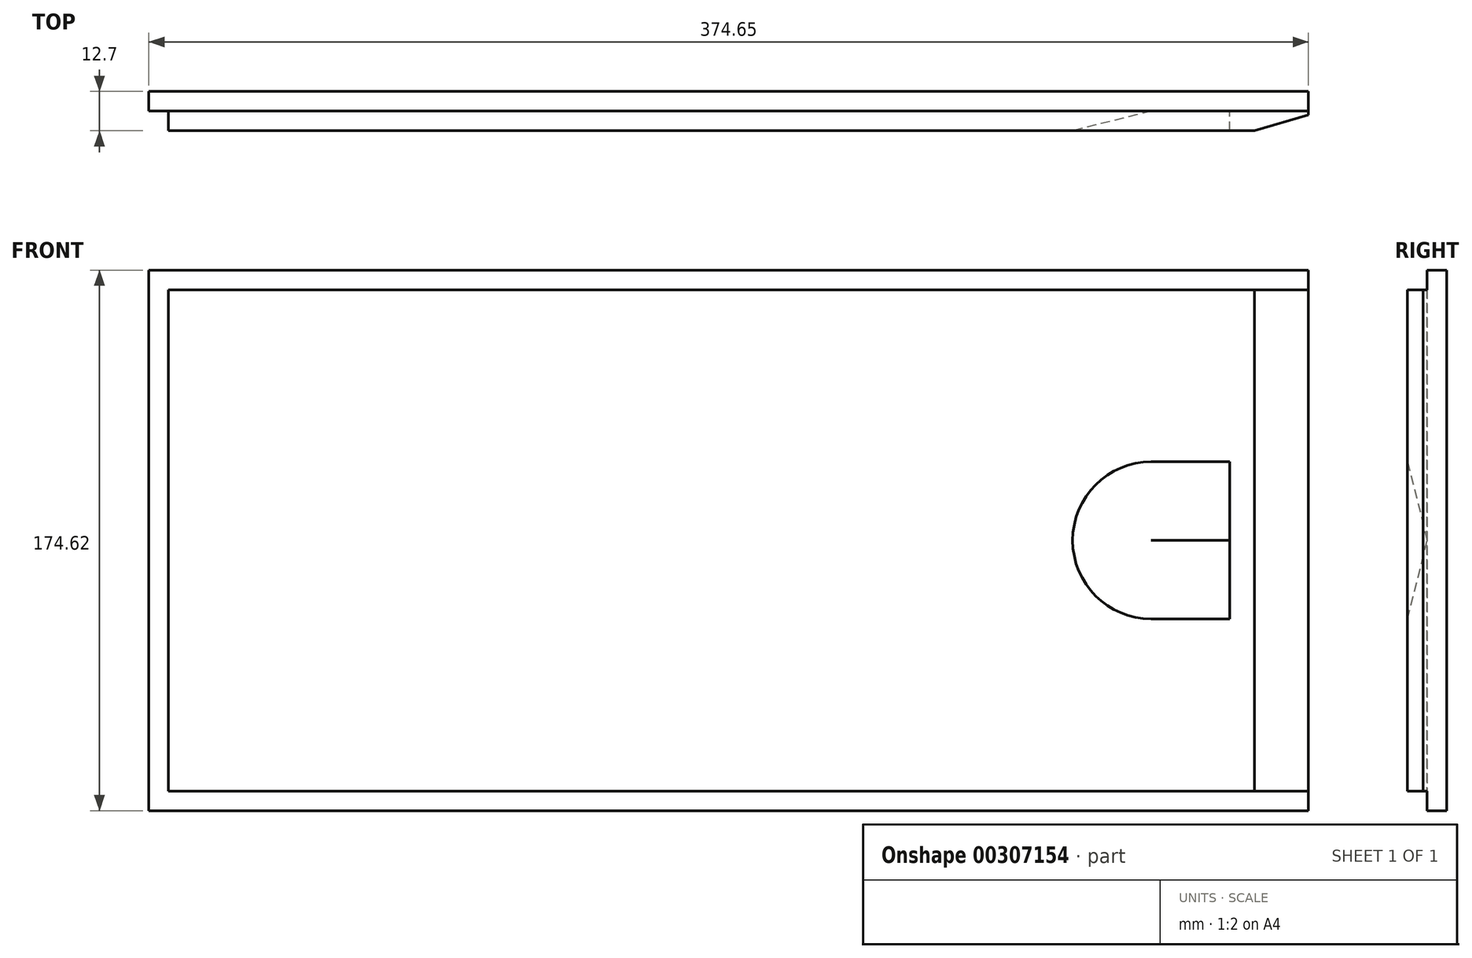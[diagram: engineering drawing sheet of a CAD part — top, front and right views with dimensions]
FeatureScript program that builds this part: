
annotation { "Feature Type Name" : "Feature", "Feature Type Description" : "" }
export const myFeature = defineFeature(function(context is Context, id is Id, definition is map)
    precondition{}
    {
        {
            var Q0;
            Q0=qCreatedBy(makeId("Front.planeOp"),FACE);
            var sketch = newSketch(context, id + "F0", { "sketchPlane" : qUnion([Q0])});
            skLineSegment(sketch, "E0.bottom", {"start": v(187.33, -87.31) * mm, "end": v(-187.33, -87.31) * mm});
            skLineSegment(sketch, "E0.top", {"start": v(187.33, 87.31) * mm, "end": v(-187.33, 87.31) * mm});
            skLineSegment(sketch, "E0.left", {"start": v(187.33, -87.31) * mm, "end": v(187.33, 87.31) * mm});
            skLineSegment(sketch, "E0.right", {"start": v(-187.33, -87.31) * mm, "end": v(-187.33, 87.31) * mm});
            skPoint(sketch, "E0.middle", {"position": v(0, 0) * mm});
            skSolve(sketch);
        }
        {
            var Q0;
            Q0=makeQuery(id+"F0.imprint","IMPRINT",FACE,{"disambiguationData":[TD([[makeQuery(id+"F0.imprint","IMPRINT",EDGE,{"derivedFrom":sQuery(id+"F0.wireOp",EDGE,"E0.bottom")}),-1.0]])]});
            extrude(context, id + "F1", {"entities" : qUnion([Q0]), "depth" : 12.7 * mm});
        }
        {
            var Q0;
            Q0=makeQuery(id+"F1.opExtrude","CAP_FACE",FACE,{"disambiguationData":[OSD([sQuery(id+"F0.wireOp",EDGE,"E0.bottom"),sQuery(id+"F0.wireOp",EDGE,"E0.top"),sQuery(id+"F0.wireOp",EDGE,"E0.left"),sQuery(id+"F0.wireOp",EDGE,"E0.right")])],"isStart":false});
            var sketch = newSketch(context, id + "F2", { "sketchPlane" : qUnion([Q0])});
            skLineSegment(sketch, "E1.bottom", {"start": v(-180.98, 87.31) * mm, "end": v(-187.33, 87.31) * mm});
            skLineSegment(sketch, "E1.top", {"start": v(-180.97, -87.31) * mm, "end": v(-187.33, -87.31) * mm});
            skLineSegment(sketch, "E1.left", {"start": v(-180.98, 87.31) * mm, "end": v(-180.97, -87.31) * mm});
            skLineSegment(sketch, "E1.right", {"start": v(-187.33, 87.31) * mm, "end": v(-187.33, -87.31) * mm});
            skLineSegment(sketch, "E2.bottom", {"start": v(-187.33, 87.31) * mm, "end": v(187.33, 87.31) * mm});
            skLineSegment(sketch, "E2.top", {"start": v(-187.33, 80.96) * mm, "end": v(187.33, 80.96) * mm});
            skLineSegment(sketch, "E2.left", {"start": v(-187.33, 87.31) * mm, "end": v(-187.33, 80.96) * mm});
            skLineSegment(sketch, "E2.right", {"start": v(187.33, 87.31) * mm, "end": v(187.33, 80.96) * mm});
            skLineSegment(sketch, "E3.bottom", {"start": v(-187.33, -80.96) * mm, "end": v(187.33, -80.96) * mm});
            skLineSegment(sketch, "E3.top", {"start": v(-187.33, -87.31) * mm, "end": v(187.33, -87.31) * mm});
            skLineSegment(sketch, "E3.left", {"start": v(-187.33, -80.96) * mm, "end": v(-187.33, -87.31) * mm});
            skLineSegment(sketch, "E3.right", {"start": v(187.33, -80.96) * mm, "end": v(187.33, -87.31) * mm});
            skLineSegment(sketch, "E4", {"start": v(169.86, 87.31) * mm, "end": v(169.86, -87.31) * mm});
            skLineSegment(sketch, "E5.bottom", {"start": v(161.93, -25.4) * mm, "end": v(111.13, -25.4) * mm});
            skLineSegment(sketch, "E5.top", {"start": v(161.93, 25.4) * mm, "end": v(111.12, 25.4) * mm});
            skLineSegment(sketch, "E5.left", {"start": v(161.93, -25.4) * mm, "end": v(161.93, 25.4) * mm});
            skLineSegment(sketch, "E5.right", {"start": v(111.13, -25.4) * mm, "end": v(111.12, 25.4) * mm});
            skPoint(sketch, "E5.middle", {"position": v(136.53, 0) * mm});
            skPoint(sketch, "E6.visualSharp", {"position": v(111.12, 25.4) * mm});
            skLineSegment(sketch, "E6.filletArc", {"start": v(111.12, 25.4) * mm, "end": v(111.12, 25.4) * mm});
            skSolve(sketch);
        }
        {
            var Q0;
            {var subQ0=sQuery(id+"F2.wireOp",EDGE,"E2.bottom");var subQ1=sQuery(id+"F2.wireOp",EDGE,"E1.left");var subQ2=makeQuery(id+"F2.imprint","INTERSECT",VERTEX,{"derivedFrom":[subQ1,subQ0]});Q0=makeQuery(id+"F2.imprint","IMPRINT",FACE,{"disambiguationData":[TD([[makeQuery(id+"F2.imprint","IMPRINT",EDGE,{"disambiguationData":[TD([[subQ2,-1.0]])],"derivedFrom":subQ1}),1.0]])]});}
            var Q1;
            {var subQ5=sQuery(id+"F2.wireOp",EDGE,"E2.left");Q1=makeQuery(id+"F2.imprint","IMPRINT",FACE,{"disambiguationData":[TD([[makeQuery(id+"F2.imprint","IMPRINT",EDGE,{"derivedFrom":subQ5}),-1.0]])]});}
            var Q2;
            {var subQ5=sQuery(id+"F2.wireOp",EDGE,"E1.right");Q2=makeQuery(id+"F2.imprint","IMPRINT",FACE,{"disambiguationData":[TD([[makeQuery(id+"F2.imprint","IMPRINT",EDGE,{"derivedFrom":subQ5}),-1.0]])]});}
            var Q3;
            {var subQ5=sQuery(id+"F2.wireOp",EDGE,"E3.left");Q3=makeQuery(id+"F2.imprint","IMPRINT",FACE,{"disambiguationData":[TD([[makeQuery(id+"F2.imprint","IMPRINT",EDGE,{"derivedFrom":subQ5}),-1.0]])]});}
            var Q4;
            {var subQ0=sQuery(id+"F2.wireOp",EDGE,"E3.top");var subQ1=sQuery(id+"F2.wireOp",EDGE,"E1.left");var subQ2=makeQuery(id+"F2.imprint","INTERSECT",VERTEX,{"derivedFrom":[subQ1,subQ0]});Q4=makeQuery(id+"F2.imprint","IMPRINT",FACE,{"disambiguationData":[TD([[makeQuery(id+"F2.imprint","IMPRINT",EDGE,{"disambiguationData":[TD([[subQ2,1.0]])],"derivedFrom":subQ1}),1.0]])]});}
            var Q5;
            {var subQ0=sQuery(id+"F2.wireOp",EDGE,"E3.right");Q5=makeQuery(id+"F2.imprint","IMPRINT",FACE,{"disambiguationData":[TD([[makeQuery(id+"F2.imprint","IMPRINT",EDGE,{"derivedFrom":subQ0}),1.0]])]});}
            var Q6;
            {var subQ0=sQuery(id+"F2.wireOp",EDGE,"E2.right");Q6=makeQuery(id+"F2.imprint","IMPRINT",FACE,{"disambiguationData":[TD([[makeQuery(id+"F2.imprint","IMPRINT",EDGE,{"derivedFrom":subQ0}),1.0]])]});}
            extrude(context, id + "F3", {"entities" : qUnion([Q0, Q1, Q2, Q3, Q4, Q5, Q6]), "operationType" : NewBodyOperationType.REMOVE, "oppositeDirection" : true, "depth" : 6.35 * mm});
        }
        {
            var Q0;
            Q0=makeQuery(id+"F1.opExtrude","CAP_EDGE",EDGE,{"disambiguationData":[OSD([sQuery(id+"F0.wireOp",EDGE,"E0.left")])],"isStart":false});
            chamfer(context, id + "F4", {"entities" : qUnion([Q0]), "chamferType" : ChamferType.TWO_OFFSETS, "width1" : 17.46 * mm, "oppositeDirection" : false, "width2" : 5.08 * mm, "tangentPropagation" : true});
        }
        {
            var Q0;
            Q0=makeQuery(id+"F2.imprint","IMPRINT",FACE,{"disambiguationData":[TD([[makeQuery(id+"F2.imprint","IMPRINT",EDGE,{"derivedFrom":sQuery(id+"F2.wireOp",EDGE,"E5.bottom")}),-1.0]])]});
            extrude(context, id + "F5", {"entities" : qUnion([Q0]), "operationType" : NewBodyOperationType.REMOVE, "oppositeDirection" : true, "depth" : 6.35 * mm});
        }
        {
            var Q0;
            Q0=makeQuery(id+"F5.boolean.opBoolean","COPY",EDGE,{"derivedFrom":makeQuery(id+"F5.opExtrude","SWEPT_EDGE",EDGE,{"disambiguationData":[OSD([sQuery(id+"F2.wireOp",EDGE,"E5.bottom"),sQuery(id+"F2.wireOp",EDGE,"E5.right")])]})});
            var Q1;
            Q1=makeQuery(id+"F5.boolean.opBoolean","COPY",EDGE,{"derivedFrom":makeQuery(id+"F5.opExtrude","SWEPT_EDGE",EDGE,{"disambiguationData":[OSD([sQuery(id+"F2.wireOp",EDGE,"E5.top"),sQuery(id+"F2.wireOp",EDGE,"E5.right")])]})});
            fillet(context, id + "F6", {"entities" : qUnion([Q0, Q1]), "radius" : 25.4 * mm, "tangentPropagation" : true, "allowEdgeOverflow" : false});
        }
        {
            var Q0;
            {var subQ0=sQuery(id+"F2.wireOp",EDGE,"E5.right");var subQ1=sQuery(id+"F2.wireOp",EDGE,"E5.bottom");Q0=makeQuery(id+"F6.opFillet","BLEND_EDGE",EDGE,{"blendedFrom":[makeQuery(id+"F5.boolean.opBoolean","COPY",EDGE,{"derivedFrom":makeQuery(id+"F5.opExtrude","SWEPT_EDGE",EDGE,{"disambiguationData":[OSD([subQ1,subQ0])]})}),makeQuery(id+"F5.boolean.opBoolean","COPY",FACE,{"derivedFrom":makeQuery(id+"F5.opExtrude","CAP_FACE",FACE,{"disambiguationData":[OSD([subQ1,sQuery(id+"F2.wireOp",EDGE,"E5.top"),sQuery(id+"F2.wireOp",EDGE,"E5.left"),subQ0])],"isStart":false})})],"blendedInto":[makeQuery(id+"F5.boolean.opBoolean","COPY",FACE,{"derivedFrom":makeQuery(id+"F5.opExtrude","CAP_FACE",FACE,{"disambiguationData":[OSD([subQ1,sQuery(id+"F2.wireOp",EDGE,"E5.top"),sQuery(id+"F2.wireOp",EDGE,"E5.left"),subQ0])],"isStart":false})})]});}
            chamfer(context, id + "F7", {"entities" : qUnion([Q0]), "chamferType" : ChamferType.TWO_OFFSETS, "width1" : 25.4 * mm, "oppositeDirection" : false, "width2" : 6.35 * mm, "tangentPropagation" : true});
        }
    });
